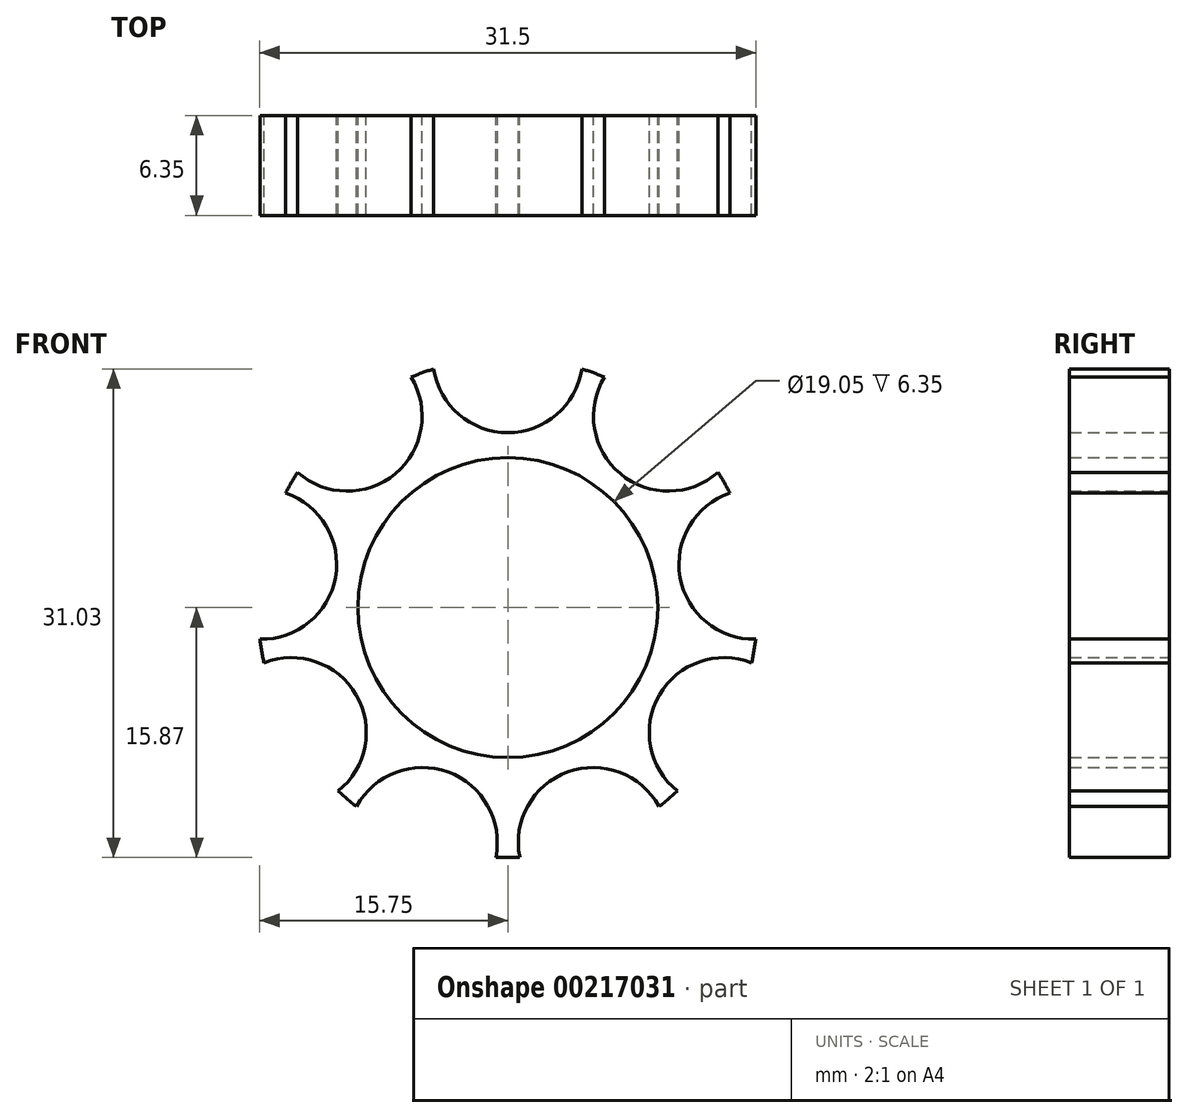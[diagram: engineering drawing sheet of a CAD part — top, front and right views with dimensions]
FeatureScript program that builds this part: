
annotation { "Feature Type Name" : "Feature", "Feature Type Description" : "" }
export const myFeature = defineFeature(function(context is Context, id is Id, definition is map)
    precondition{}
    {
        {
            var Q0;
            Q0=qCreatedBy(makeId("Front.planeOp"),FACE);
            var sketch = newSketch(context, id + "F0", { "sketchPlane" : qUnion([Q0])});
            skCircle(sketch, "E0", {"center": v(0, 0) * mm, "radius": 9.53 * mm});
            skCircle(sketch, "E1", {"center": v(0, 0) * mm, "radius": 15.88 * mm});
            skCircle(sketch, "E2", {"center": v(0, 15.88) * mm, "radius": 4.76 * mm});
            skCircle(sketch, "E3.1.0", {"center": v(-10.2, 12.16) * mm, "radius": 4.76 * mm});
            skCircle(sketch, "E3.2.0", {"center": v(-15.63, 2.76) * mm, "radius": 4.76 * mm});
            skCircle(sketch, "E3.3.0", {"center": v(-13.75, -7.94) * mm, "radius": 4.76 * mm});
            skCircle(sketch, "E3.4.0", {"center": v(-5.43, -14.92) * mm, "radius": 4.76 * mm});
            skCircle(sketch, "E3.5.0", {"center": v(5.43, -14.92) * mm, "radius": 4.76 * mm});
            skCircle(sketch, "E3.6.0", {"center": v(13.75, -7.94) * mm, "radius": 4.76 * mm});
            skCircle(sketch, "E3.7.0", {"center": v(15.63, 2.76) * mm, "radius": 4.76 * mm});
            skCircle(sketch, "E3.8.0", {"center": v(10.2, 12.16) * mm, "radius": 4.76 * mm});
            skSolve(sketch);
        }
        {
            var Q0;
            Q0=makeQuery(id+"F0.imprint","IMPRINT",FACE,{"disambiguationData":[TD([[makeQuery(id+"F0.imprint","IMPRINT",EDGE,{"derivedFrom":sQuery(id+"F0.wireOp",EDGE,"E0")}),-1.0]])]});
            extrude(context, id + "F1", {"entities" : qUnion([Q0]), "depth" : 6.35 * mm});
        }
    });
